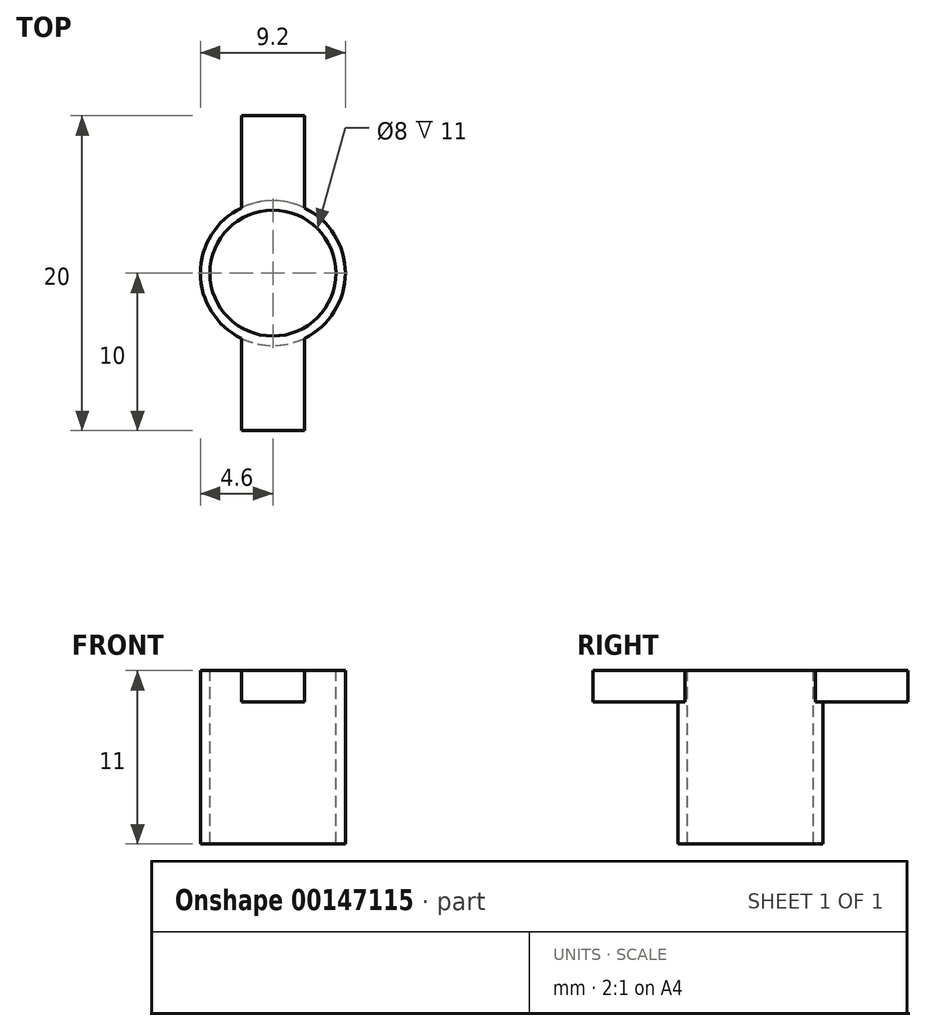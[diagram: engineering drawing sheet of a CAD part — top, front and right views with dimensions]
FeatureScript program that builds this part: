
annotation { "Feature Type Name" : "Feature", "Feature Type Description" : "" }
export const myFeature = defineFeature(function(context is Context, id is Id, definition is map)
    precondition{}
    {
        {
            var Q0;
            Q0=qCreatedBy(makeId("Top.planeOp"),FACE);
            var sketch = newSketch(context, id + "F0", { "sketchPlane" : qUnion([Q0])});
            skCircle(sketch, "E0", {"center": v(0, 0) * mm, "radius": 4.6 * mm});
            skLineSegment(sketch, "E1.bottom", {"start": v(2, -10) * mm, "end": v(-2, -10) * mm});
            skLineSegment(sketch, "E1.top", {"start": v(2, 10) * mm, "end": v(-2, 10) * mm});
            skLineSegment(sketch, "E1.left", {"start": v(2, -10) * mm, "end": v(2, 10) * mm});
            skLineSegment(sketch, "E1.right", {"start": v(-2, -10) * mm, "end": v(-2, 10) * mm});
            skCircle(sketch, "E2", {"center": v(0, 0) * mm, "radius": 4 * mm});
            skSolve(sketch);
        }
        {
            var Q0;
            {var subQ0=sQuery(id+"F0.wireOp",EDGE,"E1.right");var subQ1=sQuery(id+"F0.wireOp",EDGE,"E0");var subQ2=makeQuery(id+"F0.imprint","INTERSECT",VERTEX,{"disambiguationData":[OD(0.0)],"derivedFrom":[subQ1,subQ0]});Q0=makeQuery(id+"F0.imprint","IMPRINT",FACE,{"disambiguationData":[TD([[makeQuery(id+"F0.imprint","IMPRINT",EDGE,{"disambiguationData":[TD([[subQ2,-1.0]])],"derivedFrom":subQ1}),1.0]])]});}
            var Q1;
            {var subQ0=sQuery(id+"F0.wireOp",EDGE,"E1.right");var subQ1=sQuery(id+"F0.wireOp",EDGE,"E0");var subQ2=makeQuery(id+"F0.imprint","INTERSECT",VERTEX,{"disambiguationData":[OD(1.0)],"derivedFrom":[subQ1,subQ0]});Q1=makeQuery(id+"F0.imprint","IMPRINT",FACE,{"disambiguationData":[TD([[makeQuery(id+"F0.imprint","IMPRINT",EDGE,{"disambiguationData":[TD([[subQ2,-1.0]])],"derivedFrom":subQ1}),1.0]])]});}
            var Q2;
            {var subQ0=sQuery(id+"F0.wireOp",EDGE,"E1.left");var subQ1=sQuery(id+"F0.wireOp",EDGE,"E0");var subQ2=makeQuery(id+"F0.imprint","INTERSECT",VERTEX,{"disambiguationData":[OD(0.0)],"derivedFrom":[subQ1,subQ0]});Q2=makeQuery(id+"F0.imprint","IMPRINT",FACE,{"disambiguationData":[TD([[makeQuery(id+"F0.imprint","IMPRINT",EDGE,{"disambiguationData":[TD([[subQ2,1.0]])],"derivedFrom":subQ1}),1.0]])]});}
            var Q3;
            {var subQ0=sQuery(id+"F0.wireOp",EDGE,"E1.right");var subQ1=sQuery(id+"F0.wireOp",EDGE,"E0");var subQ2=makeQuery(id+"F0.imprint","INTERSECT",VERTEX,{"disambiguationData":[OD(0.0)],"derivedFrom":[subQ1,subQ0]});Q3=makeQuery(id+"F0.imprint","IMPRINT",FACE,{"disambiguationData":[TD([[makeQuery(id+"F0.imprint","IMPRINT",EDGE,{"disambiguationData":[TD([[subQ2,1.0]])],"derivedFrom":subQ1}),1.0]])]});}
            var Q4;
            Q4=makeQuery(id+"F0.imprint","IMPRINT",FACE,{"disambiguationData":[TD([[makeQuery(id+"F0.imprint","IMPRINT",EDGE,{"derivedFrom":sQuery(id+"F0.wireOp",EDGE,"hEtalgQT-Uj8H-44FO-WR4w-J4hWKqi9ZSPE")}),-1.0]])]});
            extrude(context, id + "F1", {"entities" : qUnion([Q0, Q1, Q2, Q3, Q4]), "oppositeDirection" : true, "depth" : 10 * mm});
        }
        {
            var Q0;
            {var subQ5=sQuery(id+"F0.wireOp",EDGE,"E1.top");Q0=makeQuery(id+"F0.imprint","IMPRINT",FACE,{"disambiguationData":[TD([[makeQuery(id+"F0.imprint","IMPRINT",EDGE,{"derivedFrom":subQ5}),1.0]])]});}
            var Q1;
            {var subQ5=sQuery(id+"F0.wireOp",EDGE,"E1.bottom");Q1=makeQuery(id+"F0.imprint","IMPRINT",FACE,{"disambiguationData":[TD([[makeQuery(id+"F0.imprint","IMPRINT",EDGE,{"derivedFrom":subQ5}),-1.0]])]});}
            var Q2;
            {var subQ0=sQuery(id+"F0.wireOp",EDGE,"E1.right");var subQ1=sQuery(id+"F0.wireOp",EDGE,"E0");var subQ2=makeQuery(id+"F0.imprint","INTERSECT",VERTEX,{"disambiguationData":[OD(0.0)],"derivedFrom":[subQ1,subQ0]});Q2=makeQuery(id+"F0.imprint","IMPRINT",FACE,{"disambiguationData":[TD([[makeQuery(id+"F0.imprint","IMPRINT",EDGE,{"disambiguationData":[TD([[subQ2,1.0]])],"derivedFrom":subQ1}),1.0]])]});}
            var Q3;
            {var subQ0=sQuery(id+"F0.wireOp",EDGE,"E1.right");var subQ1=sQuery(id+"F0.wireOp",EDGE,"E0");var subQ2=makeQuery(id+"F0.imprint","INTERSECT",VERTEX,{"disambiguationData":[OD(1.0)],"derivedFrom":[subQ1,subQ0]});Q3=makeQuery(id+"F0.imprint","IMPRINT",FACE,{"disambiguationData":[TD([[makeQuery(id+"F0.imprint","IMPRINT",EDGE,{"disambiguationData":[TD([[subQ2,-1.0]])],"derivedFrom":subQ1}),1.0]])]});}
            var Q4;
            {var subQ0=sQuery(id+"F0.wireOp",EDGE,"E1.right");var subQ1=sQuery(id+"F0.wireOp",EDGE,"E0");var subQ2=makeQuery(id+"F0.imprint","INTERSECT",VERTEX,{"disambiguationData":[OD(0.0)],"derivedFrom":[subQ1,subQ0]});Q4=makeQuery(id+"F0.imprint","IMPRINT",FACE,{"disambiguationData":[TD([[makeQuery(id+"F0.imprint","IMPRINT",EDGE,{"disambiguationData":[TD([[subQ2,-1.0]])],"derivedFrom":subQ1}),1.0]])]});}
            var Q5;
            {var subQ0=sQuery(id+"F0.wireOp",EDGE,"E1.left");var subQ1=sQuery(id+"F0.wireOp",EDGE,"E0");var subQ2=makeQuery(id+"F0.imprint","INTERSECT",VERTEX,{"disambiguationData":[OD(0.0)],"derivedFrom":[subQ1,subQ0]});Q5=makeQuery(id+"F0.imprint","IMPRINT",FACE,{"disambiguationData":[TD([[makeQuery(id+"F0.imprint","IMPRINT",EDGE,{"disambiguationData":[TD([[subQ2,1.0]])],"derivedFrom":subQ1}),1.0]])]});}
            extrude(context, id + "F2", {"entities" : qUnion([Q0, Q1, Q2, Q3, Q4, Q5]), "operationType" : NewBodyOperationType.ADD, "endBound" : BoundingType.SYMMETRIC, "depth" : 2 * mm});
        }
    });
